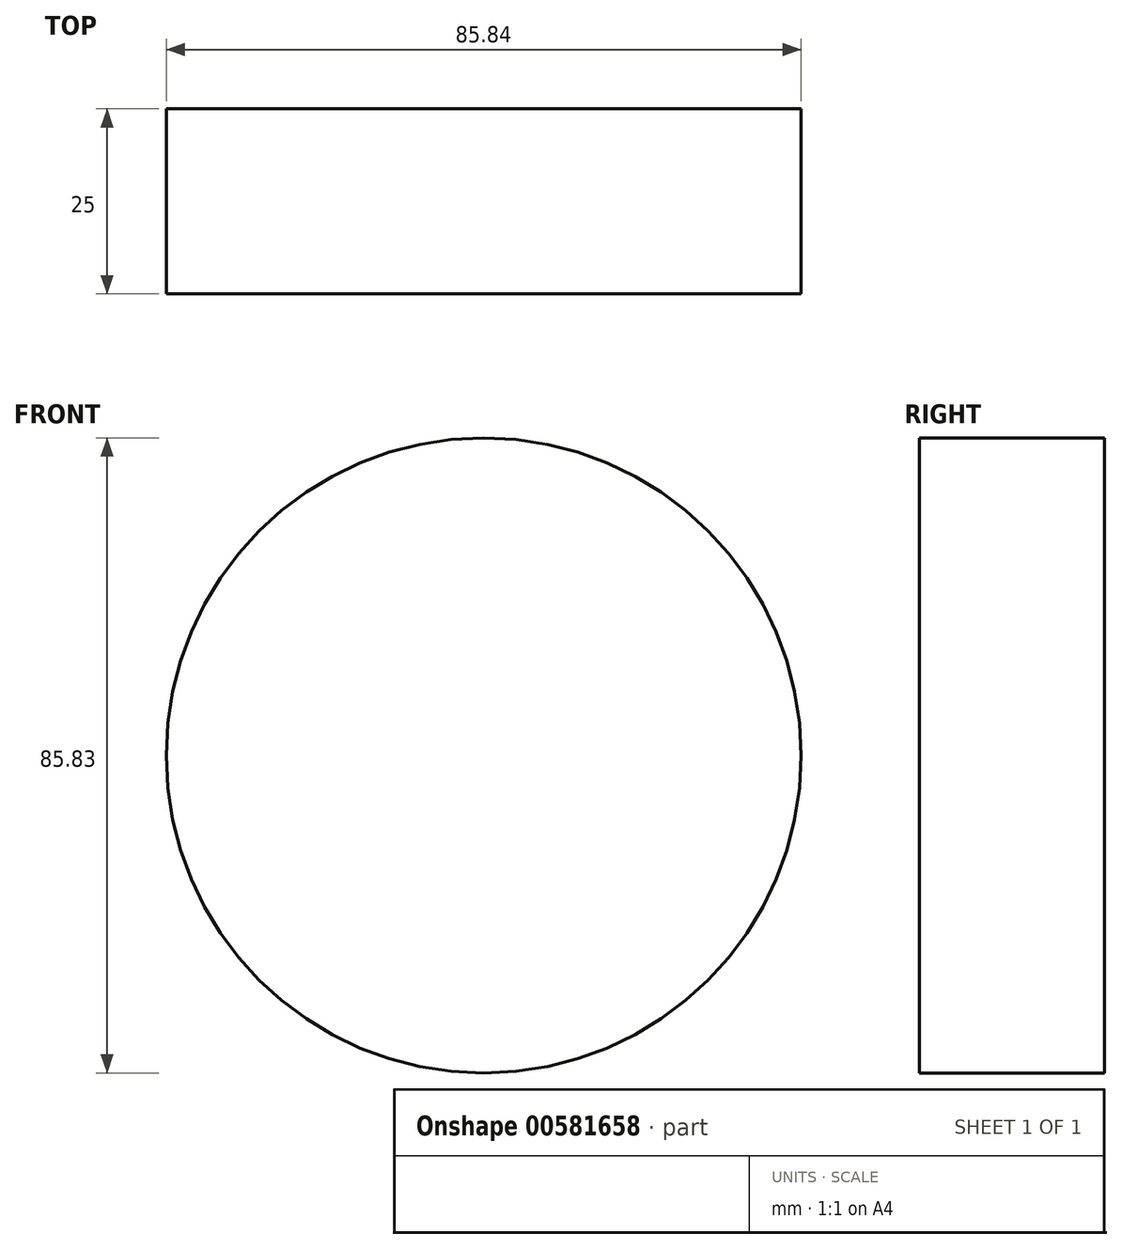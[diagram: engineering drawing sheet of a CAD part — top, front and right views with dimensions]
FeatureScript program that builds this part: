
annotation { "Feature Type Name" : "Feature", "Feature Type Description" : "" }
export const myFeature = defineFeature(function(context is Context, id is Id, definition is map)
    precondition{}
    {
        {
            var Q0;
            Q0=qCreatedBy(makeId("Front.planeOp"),FACE);
            var sketch = newSketch(context, id + "F0", { "sketchPlane" : qUnion([Q0])});
            skCircle(sketch, "E0", {"center": v(0, 67.03) * mm, "radius": 42.92 * mm});
            skSolve(sketch);
        }
        {
            var Q0;
            Q0=makeQuery(id+"F0.imprint","IMPRINT",FACE,{"disambiguationData":[TD([[makeQuery(id+"F0.imprint","IMPRINT",EDGE,{"derivedFrom":sQuery(id+"F0.wireOp",EDGE,"E0")}),1.0]])]});
            extrude(context, id + "F1", {"entities" : qUnion([Q0]), "depth" : 25 * mm, "offsetDistance" : 25 * mm});
        }
    });
